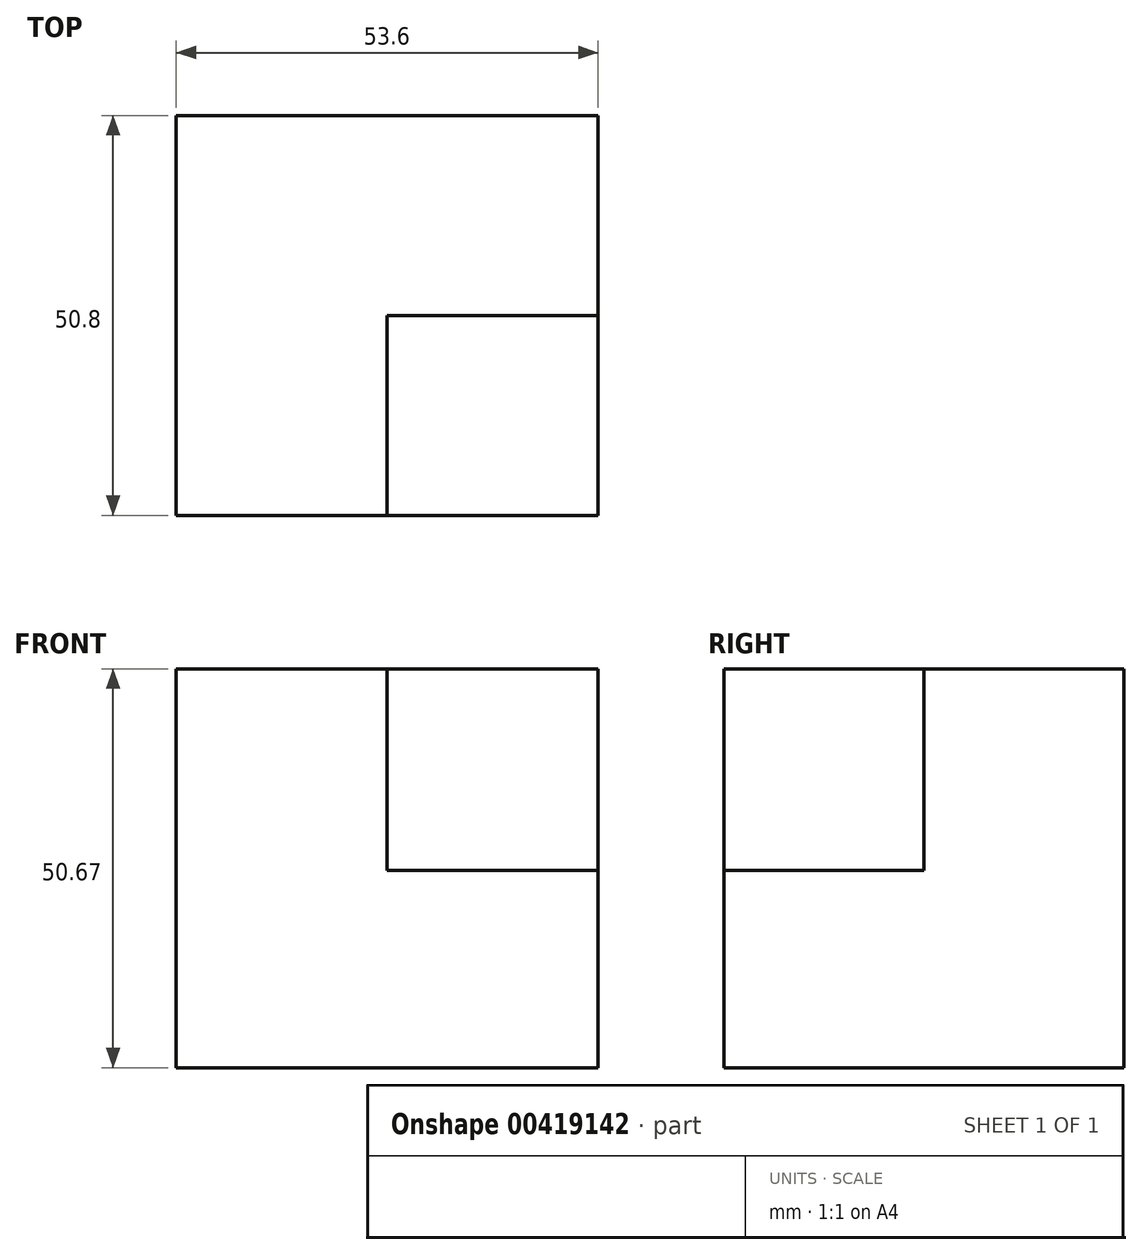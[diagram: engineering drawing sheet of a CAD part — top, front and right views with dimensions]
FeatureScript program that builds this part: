
annotation { "Feature Type Name" : "Feature", "Feature Type Description" : "" }
export const myFeature = defineFeature(function(context is Context, id is Id, definition is map)
    precondition{}
    {
        {
            var Q0;
            Q0=qCreatedBy(makeId("Front.planeOp"),FACE);
            var sketch = newSketch(context, id + "F0", { "sketchPlane" : qUnion([Q0])});
            skLineSegment(sketch, "E0.bottom", {"start": v(0, 0) * mm, "end": v(-53.6, 0) * mm});
            skLineSegment(sketch, "E0.top", {"start": v(0, 50.67) * mm, "end": v(-53.6, 50.67) * mm});
            skLineSegment(sketch, "E0.left", {"start": v(0, 0) * mm, "end": v(0, 50.67) * mm});
            skLineSegment(sketch, "E0.right", {"start": v(-53.6, 0) * mm, "end": v(-53.6, 50.67) * mm});
            skSolve(sketch);
        }
        {
            var Q0;
            Q0 = qSketchRegion(id + "F0", true);
            extrude(context, id + "F1", {"entities" : qUnion([Q0]), "depth" : 50.8 * mm});
        }
        {
            var Q0;
            Q0=makeQuery(id+"F1.opExtrude","CAP_FACE",FACE,{"disambiguationData":[OSD([sQuery(id+"F0.wireOp",EDGE,"E0.bottom"),sQuery(id+"F0.wireOp",EDGE,"E0.top"),sQuery(id+"F0.wireOp",EDGE,"E0.left"),sQuery(id+"F0.wireOp",EDGE,"E0.right")])],"isStart":false});
            var sketch = newSketch(context, id + "F2", { "sketchPlane" : qUnion([Q0])});
            skPoint(sketch, "E1.oppositeSnap0", {"position": v(-26.8, 50.67) * mm});
            skLineSegment(sketch, "E1.bottom", {"start": v(0, 50.67) * mm, "end": v(-26.8, 50.67) * mm});
            skLineSegment(sketch, "E1.top", {"start": v(0, 25.04) * mm, "end": v(-26.8, 25.04) * mm});
            skLineSegment(sketch, "E1.left", {"start": v(0, 50.67) * mm, "end": v(0, 25.04) * mm});
            skLineSegment(sketch, "E1.right", {"start": v(-26.8, 50.67) * mm, "end": v(-26.8, 25.04) * mm});
            skSolve(sketch);
        }
        {
            var Q0;
            Q0 = qSketchRegion(id + "F2", true);
            extrude(context, id + "F3", {"entities" : qUnion([Q0]), "operationType" : NewBodyOperationType.REMOVE, "oppositeDirection" : true, "depth" : 25.4 * mm});
        }
    });
